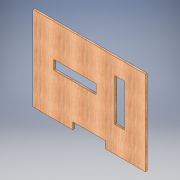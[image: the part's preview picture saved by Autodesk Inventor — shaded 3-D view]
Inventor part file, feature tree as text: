
AUTODESK INVENTOR PART (.ipt)
format: ipt  version: 2018 (Build 220112000, 112)  size: 153,088 bytes
history: native  units: in
note: dims shown in document units (in); Inventor stores cm internally (conversion verified against a paired STEP export)
features: sketch x2, other x1, extrude x1
ambient origin geometry x8: Origin, YZ Plane, XZ Plane, XY Plane, X Axis, Y Axis, Z Axis, Center Point
bodies: Solid1 (feature_tree)
feature tree (4):
  other  "Plywood"
  extrude  "SLOTS"  Depth=36.0in
  sketch  "Sketch1"  dims[d0=48.0in d1=36.0in]
  sketch  "Sketch2"  dims[d2=36.0in d3=24.0in d4=0.75in d5=0.0in d6=14.0in d7=3.0in d8=7.0in d9=18.0in d10=15.0in d11=4.0in d12=20.0in d13=0.75in d14=0.0in d15=4.0in d16=18.0in d17=8.0in d18=30.0in]
